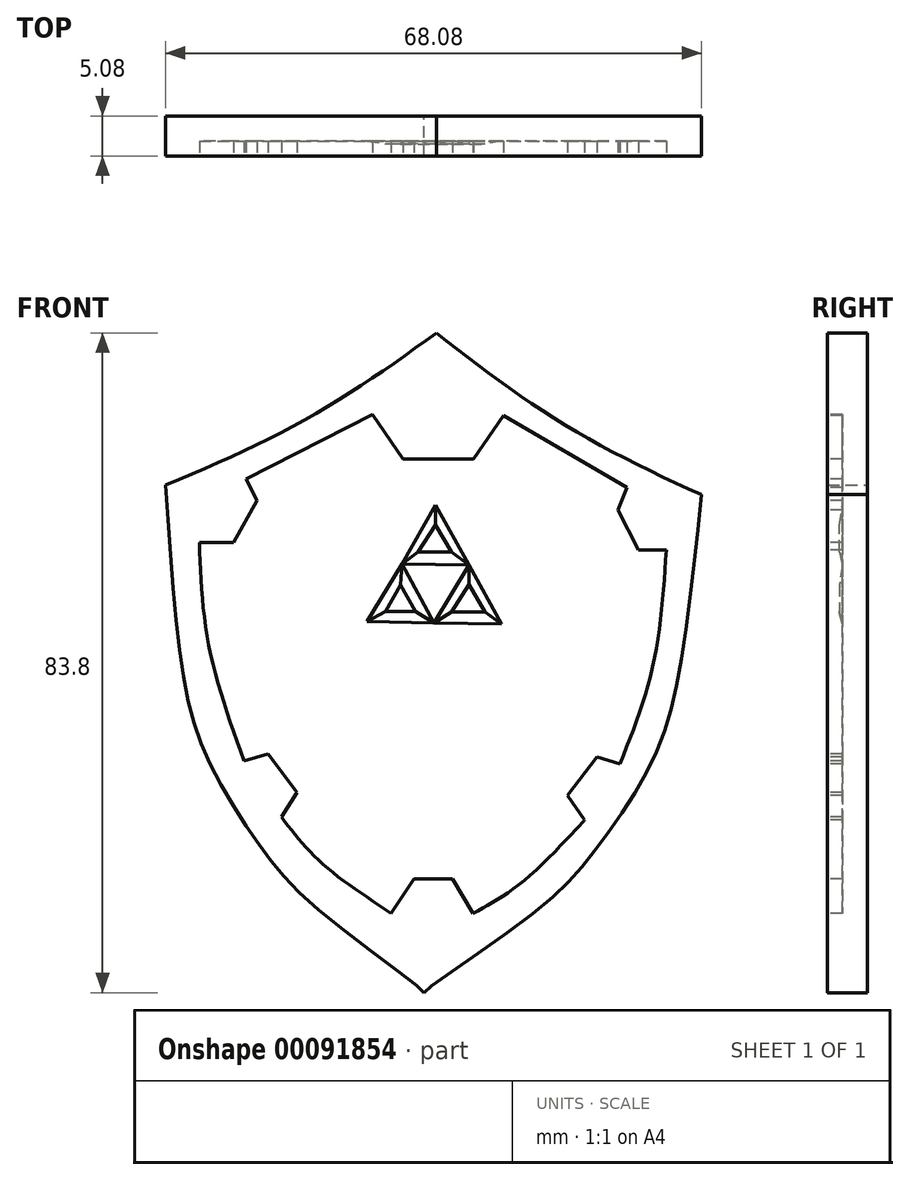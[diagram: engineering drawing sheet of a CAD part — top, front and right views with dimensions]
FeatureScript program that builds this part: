
annotation { "Feature Type Name" : "Feature", "Feature Type Description" : "" }
export const myFeature = defineFeature(function(context is Context, id is Id, definition is map)
    precondition{}
    {
        {
            var Q0;
            Q0=qCreatedBy(makeId("Front.planeOp"),FACE);
            var sketch = newSketch(context, id + "F0", { "sketchPlane" : qUnion([Q0])});
            skFitSpline(sketch, "E0", {"points": [v(76.33, 83.8) * mm, v(60.75, 73.4) * mm, v(41.92, 64.52) * mm], "startDerivative": vector(-30.88, -22.33) * mm, "endDerivative": vector(-39.17, -15.7) * mm});
            skFitSpline(sketch, "E1", {"points": [v(41.92, 64.52) * mm, v(44.1, 40.75) * mm, v(47.51, 29.18) * mm, v(54.06, 18.45) * mm, v(62, 10.02) * mm, v(74.76, 0) * mm, v(74.46, 0) * mm], "startDerivative": vector(7.03, -106.05) * mm, "endDerivative": vector(-16.3, 3.46) * mm});
            skPoint(sketch, "E2.MirrorCS.end.orphan", {"position": v(75.09, -0.01) * mm});
            skLineSegment(sketch, "E3", {"start": v(76.02, 67.13) * mm, "end": v(71.56, 67.2) * mm});
            skLineSegment(sketch, "E4", {"start": v(71.56, 67.2) * mm, "end": v(67.9, 72.92) * mm});
            skFitSpline(sketch, "E5", {"points": [v(67.9, 72.92) * mm, v(51.4, 64.6) * mm, v(51.4, 64.74) * mm], "startDerivative": vector(-26.1, -13.9) * mm, "endDerivative": vector(0.68, 2.06) * mm});
            skLineSegment(sketch, "E6", {"start": v(51.47, 64.6) * mm, "end": v(52.92, 61.34) * mm});
            skLineSegment(sketch, "E7", {"start": v(52.92, 61.34) * mm, "end": v(50.4, 56.68) * mm});
            skLineSegment(sketch, "E8", {"start": v(50.4, 56.68) * mm, "end": v(46, 56.68) * mm});
            skFitSpline(sketch, "E9", {"points": [v(46, 56.68) * mm, v(47.13, 42.96) * mm, v(51.54, 28.87) * mm], "startDerivative": vector(0.75, -27.98) * mm, "endDerivative": vector(10.27, -27.65) * mm});
            skLineSegment(sketch, "E10", {"start": v(51.54, 28.87) * mm, "end": v(54.68, 30.25) * mm});
            skLineSegment(sketch, "E11", {"start": v(54.68, 30.25) * mm, "end": v(58.2, 25.22) * mm});
            skLineSegment(sketch, "E12", {"start": v(58.2, 25.22) * mm, "end": v(56.2, 22.07) * mm});
            skFitSpline(sketch, "E13", {"points": [v(56.2, 22.07) * mm, v(61.73, 15.9) * mm, v(70.16, 9.99) * mm], "startDerivative": vector(10.7, -13.47) * mm, "endDerivative": vector(17.13, -10.74) * mm});
            skLineSegment(sketch, "E14", {"start": v(70.16, 9.99) * mm, "end": v(72.68, 14.4) * mm});
            skLineSegment(sketch, "E15", {"start": v(72.68, 14.4) * mm, "end": v(75.04, 14.35) * mm});
            skLineSegment(sketch, "E16.MirrorCS", {"start": v(76.02, 67.13) * mm, "end": v(80.49, 67.04) * mm});
            skLineSegment(sketch, "E17.MirrorCS", {"start": v(80.49, 67.04) * mm, "end": v(84.36, 72.61) * mm});
            skFitSpline(sketch, "E18.MirrorCS", {"points": [v(84.36, 72.61) * mm, v(100.52, 63.7) * mm, v(100.53, 63.82) * mm], "startDerivative": vector(25.56, -14.87) * mm, "endDerivative": vector(-0.6, 2.08) * mm});
            skLineSegment(sketch, "E19.MirrorCS", {"start": v(100.46, 63.69) * mm, "end": v(98.9, 60.48) * mm});
            skLineSegment(sketch, "E20.MirrorCS", {"start": v(98.9, 60.48) * mm, "end": v(101.23, 55.73) * mm});
            skLineSegment(sketch, "E21.MirrorCS", {"start": v(101.23, 55.73) * mm, "end": v(105.64, 55.57) * mm});
            skFitSpline(sketch, "E22.MirrorCS", {"points": [v(105.64, 55.57) * mm, v(104, 41.9) * mm, v(99.07, 27.98) * mm], "startDerivative": vector(-1.79, -27.94) * mm, "endDerivative": vector(-11.3, -27.25) * mm});
            skLineSegment(sketch, "E23.MirrorCS", {"start": v(99.07, 27.98) * mm, "end": v(95.97, 29.48) * mm});
            skLineSegment(sketch, "E24.MirrorCS", {"start": v(95.97, 29.48) * mm, "end": v(92.27, 24.58) * mm});
            skLineSegment(sketch, "E25.MirrorCS", {"start": v(92.27, 24.58) * mm, "end": v(94.16, 21.36) * mm});
            skFitSpline(sketch, "E26.MirrorCS", {"points": [v(94.16, 21.36) * mm, v(88.4, 15.4) * mm, v(79.75, 9.8) * mm], "startDerivative": vector(-11.2, -13.07) * mm, "endDerivative": vector(-17.51, -10.1) * mm});
            skLineSegment(sketch, "E27.MirrorCS", {"start": v(79.75, 9.8) * mm, "end": v(77.4, 14.3) * mm});
            skLineSegment(sketch, "E28.MirrorCS", {"start": v(77.4, 14.3) * mm, "end": v(75.04, 14.35) * mm});
            skFitSpline(sketch, "E29.MirrorCS", {"points": [v(76.33, 83.8) * mm, v(91.52, 72.83) * mm, v(110, 63.26) * mm], "startDerivative": vector(30.03, -23.46) * mm, "endDerivative": vector(38.56, -17.15) * mm});
            skFitSpline(sketch, "E30.MirrorCS", {"points": [v(110, 63.26) * mm, v(106.94, 39.58) * mm, v(103.1, 28.14) * mm, v(96.16, 17.67) * mm, v(87.91, 9.54) * mm, v(74.76, 0) * mm, v(75.09, -0.01) * mm], "startDerivative": vector(-10.98, -105.72) * mm, "endDerivative": vector(16.42, 2.85) * mm});
            skLineSegment(sketch, "E31", {"start": v(74.76, 0) * mm, "end": v(74.76, 0) * mm});
            skSolve(sketch);
        }
        {
            var Q0;
            Q0 = qSketchRegion(id + "F0", true);
            var Q1;
            Q1=makeQuery(id+"F0.imprint","IMPRINT",FACE,{"disambiguationData":[TD([[makeQuery(id+"F0.imprint","IMPRINT",EDGE,{"derivedFrom":sQuery(id+"F0.wireOp",EDGE,"E3")}),1.0]])]});
            extrude(context, id + "F1", {"entities" : qUnion([Q0, Q1]), "depth" : 5.08 * mm});
        }
        {
            var Q0;
            Q0=qCreatedBy(makeId("Front.planeOp"),FACE);
            cPlane(context, id + "F2", {"entities" : qUnion([Q0]), "cplaneType" : CPlaneType.OFFSET, "offset" : 5.08 * mm, "width" : 152.4 * mm, "height" : 152.4 * mm});
        }
        {
            var Q0;
            Q0=qCreatedBy(id+"F2.planeOp",FACE);
            var sketch = newSketch(context, id + "F3", { "sketchPlane" : qUnion([Q0])});
            skLineSegment(sketch, "E32", {"start": v(76.17, 67.78) * mm, "end": v(72.1, 67.78) * mm});
            skLineSegment(sketch, "E33", {"start": v(72.1, 67.78) * mm, "end": v(68.23, 73.47) * mm});
            skLineSegment(sketch, "E34", {"start": v(68.23, 73.47) * mm, "end": v(52.13, 65.27) * mm});
            skLineSegment(sketch, "E35", {"start": v(52.13, 65.27) * mm, "end": v(53.54, 62.5) * mm});
            skLineSegment(sketch, "E36", {"start": v(53.54, 62.5) * mm, "end": v(50.56, 57.17) * mm});
            skLineSegment(sketch, "E37", {"start": v(50.56, 57.17) * mm, "end": v(46.22, 57.17) * mm});
            skFitSpline(sketch, "E38", {"points": [v(46.22, 57.17) * mm, v(47.43, 44.05) * mm, v(51.87, 29.47) * mm], "startDerivative": vector(1.03, -27.01) * mm, "endDerivative": vector(10.15, -28.37) * mm});
            skLineSegment(sketch, "E39", {"start": v(51.87, 29.47) * mm, "end": v(54.95, 30.35) * mm});
            skLineSegment(sketch, "E40", {"start": v(54.95, 30.35) * mm, "end": v(58.61, 25.44) * mm});
            skLineSegment(sketch, "E41", {"start": v(58.61, 25.44) * mm, "end": v(56.62, 22.3) * mm});
            skFitSpline(sketch, "E42", {"points": [v(56.62, 22.3) * mm, v(61.54, 16.66) * mm, v(70.59, 10.08) * mm], "startDerivative": vector(9.68, -12.68) * mm, "endDerivative": vector(17.97, -11.8) * mm});
            skLineSegment(sketch, "E43", {"start": v(70.59, 10.08) * mm, "end": v(73.47, 14.46) * mm});
            skLineSegment(sketch, "E44", {"start": v(73.47, 14.46) * mm, "end": v(78.4, 14.46) * mm});
            skLineSegment(sketch, "E45", {"start": v(78.4, 14.46) * mm, "end": v(81, 10.08) * mm});
            skFitSpline(sketch, "E46", {"points": [v(81, 10.08) * mm, v(88.53, 15.18) * mm, v(95.12, 21.93) * mm, v(95.12, 21.93) * mm, v(95.12, 21.93) * mm], "startDerivative": vector(14, 7.53) * mm, "endDerivative": vector(-0.05, 0) * mm});
            skLineSegment(sketch, "E47", {"start": v(95.12, 21.93) * mm, "end": v(92.95, 25.08) * mm});
            skLineSegment(sketch, "E48", {"start": v(92.95, 25.08) * mm, "end": v(96.75, 29.97) * mm});
            skLineSegment(sketch, "E49", {"start": v(96.75, 29.97) * mm, "end": v(99.64, 29.03) * mm});
            skFitSpline(sketch, "E50", {"points": [v(99.64, 29.03) * mm, v(103.83, 41.56) * mm, v(105.53, 56.25) * mm], "startDerivative": vector(9.88, 25.08) * mm, "endDerivative": vector(1.97, 29) * mm});
            skLineSegment(sketch, "E51", {"start": v(105.53, 56.25) * mm, "end": v(102, 56.25) * mm});
            skLineSegment(sketch, "E52", {"start": v(102, 56.25) * mm, "end": v(99.37, 61.32) * mm});
            skLineSegment(sketch, "E53", {"start": v(99.37, 61.32) * mm, "end": v(100.56, 64.17) * mm});
            skLineSegment(sketch, "E54", {"start": v(100.56, 64.17) * mm, "end": v(84.82, 73.31) * mm});
            skLineSegment(sketch, "E55", {"start": v(84.82, 73.31) * mm, "end": v(81.04, 67.78) * mm});
            skLineSegment(sketch, "E56", {"start": v(81.04, 67.78) * mm, "end": v(76.17, 67.78) * mm});
            skSolve(sketch);
        }
        {
            var Q0;
            Q0=makeQuery(id+"F3.imprint","IMPRINT",FACE,{"disambiguationData":[TD([[makeQuery(id+"F3.imprint","IMPRINT",EDGE,{"derivedFrom":sQuery(id+"F3.wireOp",EDGE,"E32")}),1.0]])]});
            extrude(context, id + "F4", {"entities" : qUnion([Q0]), "operationType" : NewBodyOperationType.REMOVE, "oppositeDirection" : true, "depth" : 1.9 * mm});
        }
        {
            var Q0;
            Q0=makeQuery(id+"F4.boolean.opBoolean","COPY",FACE,{"derivedFrom":makeQuery(id+"F4.opExtrude","CAP_FACE",FACE,{"disambiguationData":[OSD([sQuery(id+"F3.wireOp",EDGE,"E32"),sQuery(id+"F3.wireOp",EDGE,"E33"),sQuery(id+"F3.wireOp",EDGE,"E34"),sQuery(id+"F3.wireOp",EDGE,"E35"),sQuery(id+"F3.wireOp",EDGE,"E36"),sQuery(id+"F3.wireOp",EDGE,"E37"),sQuery(id+"F3.wireOp",EDGE,"E38"),sQuery(id+"F3.wireOp",EDGE,"E39"),sQuery(id+"F3.wireOp",EDGE,"E40"),sQuery(id+"F3.wireOp",EDGE,"E41"),sQuery(id+"F3.wireOp",EDGE,"E42"),sQuery(id+"F3.wireOp",EDGE,"E43"),sQuery(id+"F3.wireOp",EDGE,"E44"),sQuery(id+"F3.wireOp",EDGE,"E45"),sQuery(id+"F3.wireOp",EDGE,"E46"),sQuery(id+"F3.wireOp",EDGE,"E47"),sQuery(id+"F3.wireOp",EDGE,"E48"),sQuery(id+"F3.wireOp",EDGE,"E49"),sQuery(id+"F3.wireOp",EDGE,"E50"),sQuery(id+"F3.wireOp",EDGE,"E51"),sQuery(id+"F3.wireOp",EDGE,"E52"),sQuery(id+"F3.wireOp",EDGE,"E53"),sQuery(id+"F3.wireOp",EDGE,"E54"),sQuery(id+"F3.wireOp",EDGE,"E55"),sQuery(id+"F3.wireOp",EDGE,"E56")])],"isStart":false})});
            var sketch = newSketch(context, id + "F5", { "sketchPlane" : qUnion([Q0])});
            skLineSegment(sketch, "E57", {"start": v(76.02, 47) * mm, "end": v(71.93, 54.44) * mm});
            skLineSegment(sketch, "E58", {"start": v(71.93, 54.44) * mm, "end": v(67.53, 47.17) * mm});
            skLineSegment(sketch, "E59", {"start": v(67.53, 47.17) * mm, "end": v(76.02, 47) * mm});
            skSolve(sketch);
        }
        {
            var Q0;
            Q0=makeQuery(id+"F5.imprint","IMPRINT",FACE,{"disambiguationData":[TD([[makeQuery(id+"F5.imprint","IMPRINT",EDGE,{"derivedFrom":sQuery(id+"F5.wireOp",EDGE,"E57")}),-1.0]])]});
            cPlane(context, id + "F6", {"entities" : qUnion([Q0]), "cplaneType" : CPlaneType.OFFSET, "offset" : 0.38 * mm, "width" : 152.4 * mm, "height" : 152.4 * mm});
        }
        {
            var Q0;
            Q0=qCreatedBy(id+"F6.planeOp",FACE);
            var sketch = newSketch(context, id + "F7", { "sketchPlane" : qUnion([Q0])});
            skLineSegment(sketch, "E60", {"start": v(71.75, 51.81) * mm, "end": v(73.65, 48.46) * mm});
            skLineSegment(sketch, "E61", {"start": v(73.65, 48.46) * mm, "end": v(69.83, 48.46) * mm});
            skLineSegment(sketch, "E62", {"start": v(71.75, 51.81) * mm, "end": v(69.83, 48.46) * mm});
            skSolve(sketch);
        }
        {
            var Q1;
            Q1 = qSketchRegion(id + "F5", true);
            var Q2;
            Q2 = qSketchRegion(id + "F7", true);
            loft(context, id + "F8", {"operationType" : NewBodyOperationType.ADD, "sheetProfilesArray" : [{ "sheetProfileEntities" : qUnion([Q1]) }, { "sheetProfileEntities" : qUnion([Q2]) }]});
        }
        {
            var Q0;
            Q0=makeQuery(id+"F4.boolean.opBoolean","COPY",FACE,{"derivedFrom":makeQuery(id+"F4.opExtrude","CAP_FACE",FACE,{"disambiguationData":[OSD([sQuery(id+"F3.wireOp",EDGE,"E32"),sQuery(id+"F3.wireOp",EDGE,"E33"),sQuery(id+"F3.wireOp",EDGE,"E34"),sQuery(id+"F3.wireOp",EDGE,"E35"),sQuery(id+"F3.wireOp",EDGE,"E36"),sQuery(id+"F3.wireOp",EDGE,"E37"),sQuery(id+"F3.wireOp",EDGE,"E38"),sQuery(id+"F3.wireOp",EDGE,"E39"),sQuery(id+"F3.wireOp",EDGE,"E40"),sQuery(id+"F3.wireOp",EDGE,"E41"),sQuery(id+"F3.wireOp",EDGE,"E42"),sQuery(id+"F3.wireOp",EDGE,"E43"),sQuery(id+"F3.wireOp",EDGE,"E44"),sQuery(id+"F3.wireOp",EDGE,"E45"),sQuery(id+"F3.wireOp",EDGE,"E46"),sQuery(id+"F3.wireOp",EDGE,"E47"),sQuery(id+"F3.wireOp",EDGE,"E48"),sQuery(id+"F3.wireOp",EDGE,"E49"),sQuery(id+"F3.wireOp",EDGE,"E50"),sQuery(id+"F3.wireOp",EDGE,"E51"),sQuery(id+"F3.wireOp",EDGE,"E52"),sQuery(id+"F3.wireOp",EDGE,"E53"),sQuery(id+"F3.wireOp",EDGE,"E54"),sQuery(id+"F3.wireOp",EDGE,"E55"),sQuery(id+"F3.wireOp",EDGE,"E56")])],"isStart":false})});
            var sketch = newSketch(context, id + "F9", { "sketchPlane" : qUnion([Q0])});
            skLineSegment(sketch, "E63", {"start": v(80.5, 54.32) * mm, "end": v(76.02, 47) * mm});
            skLineSegment(sketch, "E64", {"start": v(76.02, 47) * mm, "end": v(84.59, 46.81) * mm});
            skLineSegment(sketch, "E65", {"start": v(84.59, 46.81) * mm, "end": v(80.5, 54.32) * mm});
            skSolve(sketch);
        }
        {
            var Q0;
            Q0=makeQuery(id+"F8.opLoft","CAP_FACE",FACE,{"disambiguationData":[OSD([makeQuery(id+"F7.imprint","IMPRINT",FACE,{"disambiguationData":[TD([[makeQuery(id+"F7.imprint","IMPRINT",EDGE,{"derivedFrom":sQuery(id+"F7.wireOp",EDGE,"E60")}),-1.0]])]})])],"isStart":true});
            var sketch = newSketch(context, id + "F10", { "sketchPlane" : qUnion([Q0])});
            skLineSegment(sketch, "E66", {"start": v(80.48, 51.85) * mm, "end": v(78.26, 48.36) * mm});
            skLineSegment(sketch, "E67", {"start": v(78.26, 48.36) * mm, "end": v(82.48, 48.36) * mm});
            skLineSegment(sketch, "E68", {"start": v(82.48, 48.36) * mm, "end": v(80.48, 51.85) * mm});
            skSolve(sketch);
        }
        {
            var Q1;
            Q1 = qSketchRegion(id + "F9", true);
            var Q2;
            Q2 = qSketchRegion(id + "F10", true);
            loft(context, id + "F11", {"operationType" : NewBodyOperationType.ADD, "sheetProfilesArray" : [{ "sheetProfileEntities" : qUnion([Q1]) }, { "sheetProfileEntities" : qUnion([Q2]) }]});
        }
        {
            var Q0;
            Q0=makeQuery(id+"F4.boolean.opBoolean","COPY",FACE,{"derivedFrom":makeQuery(id+"F4.opExtrude","CAP_FACE",FACE,{"disambiguationData":[OSD([sQuery(id+"F3.wireOp",EDGE,"E32"),sQuery(id+"F3.wireOp",EDGE,"E33"),sQuery(id+"F3.wireOp",EDGE,"E34"),sQuery(id+"F3.wireOp",EDGE,"E35"),sQuery(id+"F3.wireOp",EDGE,"E36"),sQuery(id+"F3.wireOp",EDGE,"E37"),sQuery(id+"F3.wireOp",EDGE,"E38"),sQuery(id+"F3.wireOp",EDGE,"E39"),sQuery(id+"F3.wireOp",EDGE,"E40"),sQuery(id+"F3.wireOp",EDGE,"E41"),sQuery(id+"F3.wireOp",EDGE,"E42"),sQuery(id+"F3.wireOp",EDGE,"E43"),sQuery(id+"F3.wireOp",EDGE,"E44"),sQuery(id+"F3.wireOp",EDGE,"E45"),sQuery(id+"F3.wireOp",EDGE,"E46"),sQuery(id+"F3.wireOp",EDGE,"E47"),sQuery(id+"F3.wireOp",EDGE,"E48"),sQuery(id+"F3.wireOp",EDGE,"E49"),sQuery(id+"F3.wireOp",EDGE,"E50"),sQuery(id+"F3.wireOp",EDGE,"E51"),sQuery(id+"F3.wireOp",EDGE,"E52"),sQuery(id+"F3.wireOp",EDGE,"E53"),sQuery(id+"F3.wireOp",EDGE,"E54"),sQuery(id+"F3.wireOp",EDGE,"E55"),sQuery(id+"F3.wireOp",EDGE,"E56")])],"isStart":false})});
            var sketch = newSketch(context, id + "F12", { "sketchPlane" : qUnion([Q0])});
            skLineSegment(sketch, "E69", {"start": v(71.93, 54.44) * mm, "end": v(80.5, 54.32) * mm});
            skLineSegment(sketch, "E70", {"start": v(80.5, 54.32) * mm, "end": v(76.21, 61.93) * mm});
            skLineSegment(sketch, "E71", {"start": v(76.21, 61.93) * mm, "end": v(71.93, 54.44) * mm});
            skSolve(sketch);
        }
        {
            var Q0;
            Q0=qCreatedBy(id+"F6.planeOp",FACE);
            var sketch = newSketch(context, id + "F13", { "sketchPlane" : qUnion([Q0])});
            skLineSegment(sketch, "E72", {"start": v(73.97, 55.98) * mm, "end": v(78.23, 55.98) * mm});
            skLineSegment(sketch, "E73", {"start": v(78.23, 55.98) * mm, "end": v(76.2, 59.4) * mm});
            skLineSegment(sketch, "E74", {"start": v(76.2, 59.4) * mm, "end": v(73.97, 55.98) * mm});
            skSolve(sketch);
        }
        {
            var Q1;
            Q1 = qSketchRegion(id + "F13", true);
            var Q2;
            Q2 = qSketchRegion(id + "F12", true);
            loft(context, id + "F14", {"operationType" : NewBodyOperationType.ADD, "sheetProfilesArray" : [{ "sheetProfileEntities" : qUnion([Q1]) }, { "sheetProfileEntities" : qUnion([Q2]) }]});
        }
    });
